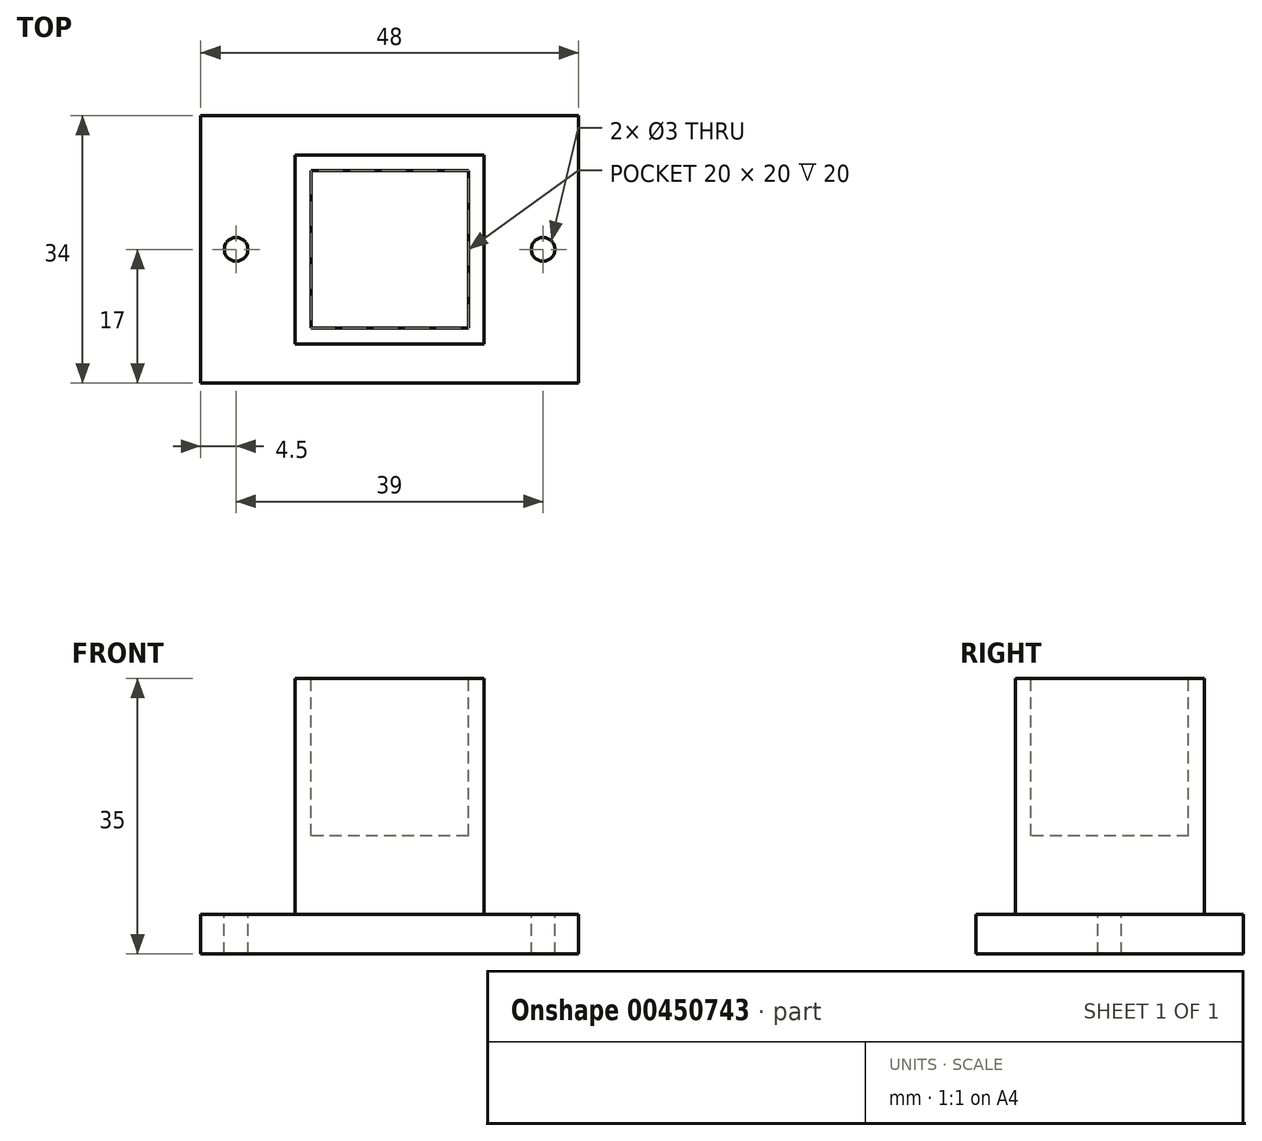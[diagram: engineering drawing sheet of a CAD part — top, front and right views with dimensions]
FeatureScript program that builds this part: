
annotation { "Feature Type Name" : "Feature", "Feature Type Description" : "" }
export const myFeature = defineFeature(function(context is Context, id is Id, definition is map)
    precondition{}
    {
        {
            var Q0;
            Q0=qCreatedBy(makeId("Top.planeOp"),FACE);
            var sketch = newSketch(context, id + "F0", { "sketchPlane" : qUnion([Q0])});
            skLineSegment(sketch, "E0.bottom", {"start": v(24, 17) * mm, "end": v(-24, 17) * mm});
            skLineSegment(sketch, "E0.top", {"start": v(24, -17) * mm, "end": v(-24, -17) * mm});
            skLineSegment(sketch, "E0.left", {"start": v(24, 17) * mm, "end": v(24, -17) * mm});
            skLineSegment(sketch, "E0.right", {"start": v(-24, 17) * mm, "end": v(-24, -17) * mm});
            skPoint(sketch, "E0.middle", {"position": v(0, 0) * mm});
            skSolve(sketch);
        }
        {
            var Q0;
            Q0 = qSketchRegion(id + "F0", true);
            extrude(context, id + "F1", {"entities" : qUnion([Q0]), "depth" : -5 * mm});
        }
        {
            var Q0;
            Q0=makeQuery(id+"F1.opExtrude","CAP_FACE",FACE,{"disambiguationData":[OSD([sQuery(id+"F0.wireOp",EDGE,"E0.bottom"),sQuery(id+"F0.wireOp",EDGE,"E0.top"),sQuery(id+"F0.wireOp",EDGE,"E0.left"),sQuery(id+"F0.wireOp",EDGE,"E0.right")])],"isStart":true});
            var sketch = newSketch(context, id + "F2", { "sketchPlane" : qUnion([Q0])});
            skLineSegment(sketch, "E1", {"start": v(0, 0) * mm, "end": v(-19.5, 0) * mm});
            skCircle(sketch, "E2", {"center": v(-19.5, 0) * mm, "radius": 1.5 * mm});
            skLineSegment(sketch, "E3", {"start": v(0, 0) * mm, "end": v(19.5, 0) * mm});
            skCircle(sketch, "E4", {"center": v(19.5, 0) * mm, "radius": 1.5 * mm});
            skSolve(sketch);
        }
        {
            var Q0;
            Q0 = qSketchRegion(id + "F2", true);
            extrude(context, id + "F3", {"entities" : qUnion([Q0]), "operationType" : NewBodyOperationType.REMOVE, "oppositeDirection" : true, "depth" : 5 * mm});
        }
        {
            var Q0;
            Q0=makeQuery(id+"F1.opExtrude","CAP_FACE",FACE,{"disambiguationData":[OSD([sQuery(id+"F0.wireOp",EDGE,"E0.bottom"),sQuery(id+"F0.wireOp",EDGE,"E0.top"),sQuery(id+"F0.wireOp",EDGE,"E0.left"),sQuery(id+"F0.wireOp",EDGE,"E0.right")])],"isStart":true});
            var sketch = newSketch(context, id + "F4", { "sketchPlane" : qUnion([Q0])});
            skLineSegment(sketch, "E5.bottom", {"start": v(12, 12) * mm, "end": v(-12, 12) * mm});
            skLineSegment(sketch, "E5.top", {"start": v(12, -12) * mm, "end": v(-12, -12) * mm});
            skLineSegment(sketch, "E5.left", {"start": v(12, 12) * mm, "end": v(12, -12) * mm});
            skLineSegment(sketch, "E5.right", {"start": v(-12, 12) * mm, "end": v(-12, -12) * mm});
            skPoint(sketch, "E5.middle", {"position": v(0, 0) * mm});
            skSolve(sketch);
        }
        {
            var Q0;
            Q0 = qSketchRegion(id + "F4", true);
            extrude(context, id + "F5", {"entities" : qUnion([Q0]), "operationType" : NewBodyOperationType.ADD, "depth" : 30 * mm});
        }
        {
            var Q0;
            Q0=makeQuery(id+"F5.opExtrude","CAP_FACE",FACE,{"disambiguationData":[OSD([sQuery(id+"F4.wireOp",EDGE,"E5.bottom"),sQuery(id+"F4.wireOp",EDGE,"E5.top"),sQuery(id+"F4.wireOp",EDGE,"E5.left"),sQuery(id+"F4.wireOp",EDGE,"E5.right")])],"isStart":false});
            var sketch = newSketch(context, id + "F6", { "sketchPlane" : qUnion([Q0])});
            skLineSegment(sketch, "E6.bottom", {"start": v(10, 10) * mm, "end": v(-10, 10) * mm});
            skLineSegment(sketch, "E6.top", {"start": v(10, -10) * mm, "end": v(-10, -10) * mm});
            skLineSegment(sketch, "E6.left", {"start": v(10, 10) * mm, "end": v(10, -10) * mm});
            skLineSegment(sketch, "E6.right", {"start": v(-10, 10) * mm, "end": v(-10, -10) * mm});
            skPoint(sketch, "E6.middle", {"position": v(0, 0) * mm});
            skSolve(sketch);
        }
        {
            var Q0;
            Q0 = qSketchRegion(id + "F6", true);
            extrude(context, id + "F7", {"entities" : qUnion([Q0]), "operationType" : NewBodyOperationType.REMOVE, "oppositeDirection" : true, "depth" : 20 * mm});
        }
    });
